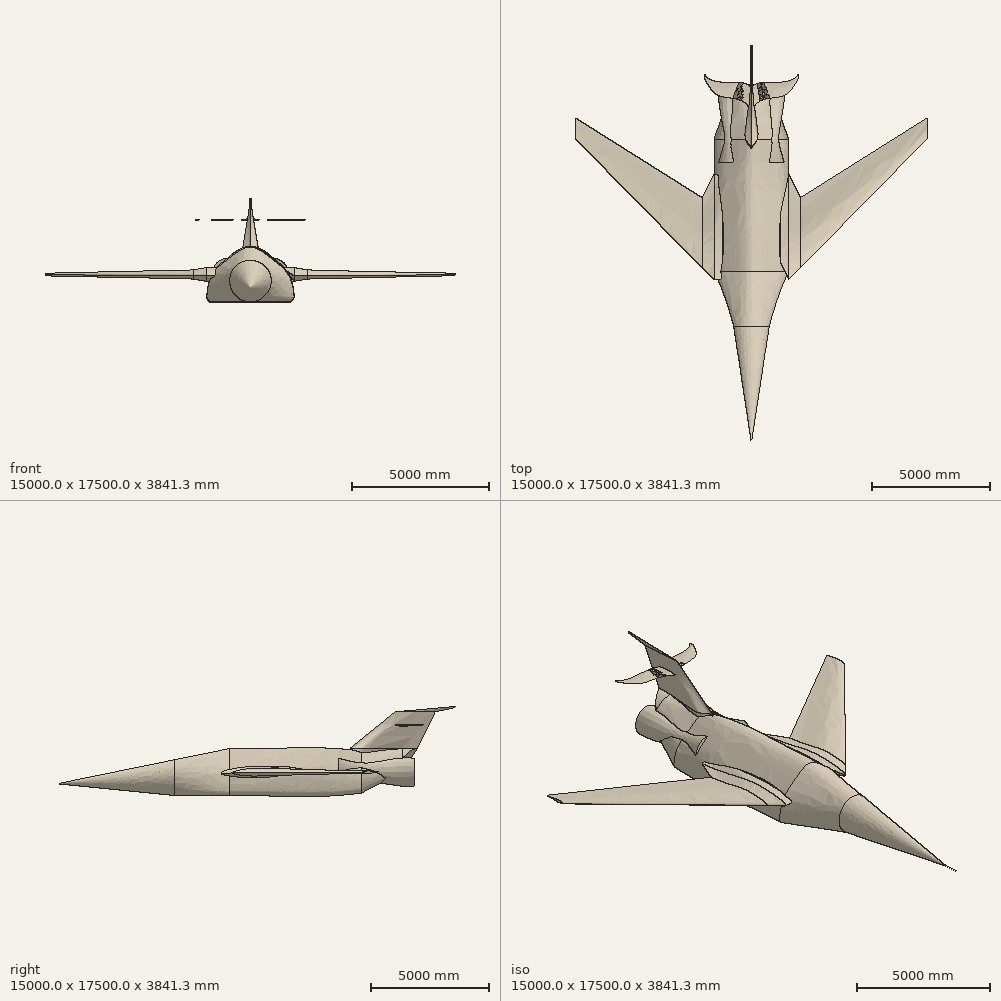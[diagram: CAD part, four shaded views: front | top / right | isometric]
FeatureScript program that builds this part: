
annotation { "Feature Type Name" : "Feature", "Feature Type Description" : "" }
export const myFeature = defineFeature(function(context is Context, id is Id, definition is map)
    precondition{}
    {
        {
            var Q0;
            Q0=qCreatedBy(makeId("Right.planeOp"),FACE);
            var sketch = newSketch(context, id + "F0", { "sketchPlane" : qUnion([Q0])});
            skLineSegment(sketch, "E0", {"start": v(0, 0) * mm, "end": v(-1750, 0) * mm});
            skLineSegment(sketch, "E1", {"start": v(-1750, 0) * mm, "end": v(-3500, 0) * mm});
            skLineSegment(sketch, "E2", {"start": v(-3500, 0) * mm, "end": v(-3500, -1000) * mm});
            skLineSegment(sketch, "E3", {"start": v(-3500, -1000) * mm, "end": v(-8500, -1000) * mm});
            skLineSegment(sketch, "E4", {"start": v(-8500, -1000) * mm, "end": v(-8500, -499.31) * mm});
            skLineSegment(sketch, "E5", {"start": v(-1151.4, 0) * mm, "end": v(-1151.4, 1000) * mm});
            skLineSegment(sketch, "E6", {"start": v(-1151.4, 1000) * mm, "end": v(-8500, -499.31) * mm});
            skLineSegment(sketch, "E7", {"start": v(-8500, -499.31) * mm, "end": v(-3500, -1000) * mm});
            skLineSegment(sketch, "E8", {"start": v(-3500, 0) * mm, "end": v(-3500, 520.82) * mm});
            skLineSegment(sketch, "E9", {"start": v(-8500, -499.31) * mm, "end": v(-8450, -499.31) * mm});
            skLineSegment(sketch, "E10", {"start": v(-8450, -499.31) * mm, "end": v(-8450, -489.1) * mm});
            skLineSegment(sketch, "E11", {"start": v(-8450, -499.31) * mm, "end": v(-8450, -504.32) * mm});
            skSolve(sketch);
        }
        {
            var Q0;
            Q0=sQuery(id+"F0.wireOp",EDGE,"E5");
            cPlane(context, id + "F1", {"entities" : qUnion([Q0]), "cplaneType" : CPlaneType.LINE_ANGLE, "offset" : 25 * mm, "angle" : 90 * degree, "oppositeDirection" : true, "width" : 150 * mm, "height" : 150 * mm});
        }
        {
            var Q0;
            Q0=qCreatedBy(id+"F1.planeOp",FACE);
            var sketch = newSketch(context, id + "F2", { "sketchPlane" : qUnion([Q0])});
            skLineSegment(sketch, "E12.top", {"start": v(-1394.2, -1000) * mm, "end": v(1394.2, -1000) * mm});
            skPoint(sketch, "E12.middle", {"position": v(0, 0) * mm});
            skFitSpline(sketch, "E13", {"points": [v(-1600, -1000) * mm, v(-848, 530) * mm, v(0, 1000) * mm, v(848, 530) * mm, v(1600, -1000) * mm], "startDerivative": vector(0, 10524.75) * mm, "endDerivative": vector(0, -10524.75) * mm});
            skArc(sketch, "E14", {"start": v(-735.27, 618.52) * mm, "mid": v(-1273.27, 435.52) * mm, "end": v(-1440.68, -107.53) * mm});
            skArc(sketch, "E15", {"start": v(1440.68, -107.53) * mm, "mid": v(1273.27, 435.52) * mm, "end": v(735.27, 618.52) * mm});
            skFitSpline(sketch, "E16.trimOffspring", {"points": [v(-1600, -1000) * mm, v(-848, 530) * mm, v(0, 1000) * mm, v(848, 530) * mm, v(1600, -1000) * mm], "startDerivative": vector(0, 10524.75) * mm, "endDerivative": vector(0, -10524.75) * mm});
            skFitSpline(sketch, "E17.trimOffspring", {"points": [v(-1600, -1000) * mm, v(-848, 530) * mm, v(0, 1000) * mm, v(848, 530) * mm, v(1600, -1000) * mm], "startDerivative": vector(0, 10524.75) * mm, "endDerivative": vector(0, -10524.75) * mm});
            skArc(sketch, "E18.filletArc", {"start": v(-1593.82, -787.83) * mm, "mid": v(-1539.85, -937.05) * mm, "end": v(-1394.2, -1000) * mm});
            skArc(sketch, "E19.filletArc", {"start": v(1394.2, -1000) * mm, "mid": v(1539.85, -937.05) * mm, "end": v(1593.82, -787.83) * mm});
            skSolve(sketch);
        }
        {
            var Q0;
            Q0=qCreatedBy(makeId("Front.planeOp"),FACE);
            var sketch = newSketch(context, id + "F3", { "sketchPlane" : qUnion([Q0])});
            skLineSegment(sketch, "E20.top", {"start": v(-1394.2, -1000) * mm, "end": v(1394.2, -1000) * mm});
            skPoint(sketch, "E20.middle", {"position": v(0, 0) * mm});
            skFitSpline(sketch, "E21", {"points": [v(-1600, -1000) * mm, v(-848, 530) * mm, v(0, 1000) * mm, v(848, 530) * mm, v(1600, -1000) * mm], "startDerivative": vector(0, 10524.75) * mm, "endDerivative": vector(0, -10524.75) * mm});
            skArc(sketch, "E22", {"start": v(-735.27, 618.52) * mm, "mid": v(-1273.27, 435.52) * mm, "end": v(-1440.68, -107.53) * mm});
            skArc(sketch, "E23", {"start": v(1440.68, -107.53) * mm, "mid": v(1273.27, 435.52) * mm, "end": v(735.27, 618.52) * mm});
            skFitSpline(sketch, "E24.trimOffspring", {"points": [v(-1600, -1000) * mm, v(-848, 530) * mm, v(0, 1000) * mm, v(848, 530) * mm, v(1600, -1000) * mm], "startDerivative": vector(0, 10524.75) * mm, "endDerivative": vector(0, -10524.75) * mm});
            skFitSpline(sketch, "E25.trimOffspring", {"points": [v(-1600, -1000) * mm, v(-848, 530) * mm, v(0, 1000) * mm, v(848, 530) * mm, v(1600, -1000) * mm], "startDerivative": vector(0, 10524.75) * mm, "endDerivative": vector(0, -10524.75) * mm});
            skArc(sketch, "E26.filletArc", {"start": v(-1593.82, -787.83) * mm, "mid": v(-1539.85, -937.05) * mm, "end": v(-1394.2, -1000) * mm});
            skArc(sketch, "E27.filletArc", {"start": v(1394.2, -1000) * mm, "mid": v(1539.85, -937.05) * mm, "end": v(1593.82, -787.83) * mm});
            skSolve(sketch);
        }
        {
            var Q0;
            Q0=qCreatedBy(makeId("Front.planeOp"),FACE);
            cPlane(context, id + "F4", {"entities" : qUnion([Q0]), "cplaneType" : CPlaneType.OFFSET, "offset" : 3500 * mm, "oppositeDirection" : true, "width" : 150 * mm, "height" : 150 * mm});
        }
        {
            var Q0;
            Q0=qCreatedBy(id+"F4.planeOp",FACE);
            var sketch = newSketch(context, id + "F5", { "sketchPlane" : qUnion([Q0])});
            skLineSegment(sketch, "E28.top", {"start": v(-1394.2, -1000) * mm, "end": v(1394.2, -1000) * mm});
            skPoint(sketch, "E28.middle", {"position": v(0, 0) * mm});
            skFitSpline(sketch, "E29", {"points": [v(-1600, -1000) * mm, v(-848, 530) * mm, v(0, 1000) * mm, v(848, 530) * mm, v(1600, -1000) * mm], "startDerivative": vector(0, 10524.75) * mm, "endDerivative": vector(0, -10524.75) * mm});
            skArc(sketch, "E30", {"start": v(-735.27, 618.52) * mm, "mid": v(-1273.27, 435.52) * mm, "end": v(-1440.68, -107.53) * mm});
            skArc(sketch, "E31", {"start": v(1440.68, -107.53) * mm, "mid": v(1273.27, 435.52) * mm, "end": v(735.27, 618.52) * mm});
            skFitSpline(sketch, "E32.trimOffspring", {"points": [v(-1600, -1000) * mm, v(-848, 530) * mm, v(0, 1000) * mm, v(848, 530) * mm, v(1600, -1000) * mm], "startDerivative": vector(0, 10524.75) * mm, "endDerivative": vector(0, -10524.75) * mm});
            skFitSpline(sketch, "E33.trimOffspring", {"points": [v(-1600, -1000) * mm, v(-848, 530) * mm, v(0, 1000) * mm, v(848, 530) * mm, v(1600, -1000) * mm], "startDerivative": vector(0, 10524.75) * mm, "endDerivative": vector(0, -10524.75) * mm});
            skArc(sketch, "E34.filletArc", {"start": v(-1593.82, -787.83) * mm, "mid": v(-1539.85, -937.05) * mm, "end": v(-1394.2, -1000) * mm});
            skArc(sketch, "E35.filletArc", {"start": v(1394.2, -1000) * mm, "mid": v(1539.85, -937.05) * mm, "end": v(1593.82, -787.83) * mm});
            skSolve(sketch);
        }
        {
            var Q0;
            Q0=qCreatedBy(makeId("Front.planeOp"),FACE);
            cPlane(context, id + "F6", {"entities" : qUnion([Q0]), "cplaneType" : CPlaneType.OFFSET, "offset" : 4500 * mm, "oppositeDirection" : true, "width" : 150 * mm, "height" : 150 * mm});
        }
        {
            var Q0;
            Q0=qCreatedBy(id+"F6.planeOp",FACE);
            var sketch = newSketch(context, id + "F7", { "sketchPlane" : qUnion([Q0])});
            skLineSegment(sketch, "E36.top", {"start": v(-1413.07, -900) * mm, "end": v(1413.07, -900) * mm});
            skPoint(sketch, "E36.middle", {"position": v(0, 0) * mm});
            skFitSpline(sketch, "E37", {"points": [v(-1600, -900) * mm, v(-784.42, 441.24) * mm, v(0, 900) * mm, v(784.42, 441.24) * mm, v(1600, -900) * mm], "startDerivative": vector(0, 9508.62) * mm, "endDerivative": vector(0, -9508.62) * mm});
            skArc(sketch, "E38", {"start": v(-719.25, 488.69) * mm, "mid": v(-1131.76, 394.84) * mm, "end": v(-1324.66, 18.33) * mm});
            skArc(sketch, "E39", {"start": v(1324.66, 18.33) * mm, "mid": v(1131.76, 394.84) * mm, "end": v(719.25, 488.69) * mm});
            skFitSpline(sketch, "E40.trimOffspring", {"points": [v(-1600, -900) * mm, v(-784.42, 441.24) * mm, v(0, 900) * mm, v(784.42, 441.24) * mm, v(1600, -900) * mm], "startDerivative": vector(0, 9508.62) * mm, "endDerivative": vector(0, -9508.62) * mm});
            skFitSpline(sketch, "E41.trimOffspring", {"points": [v(-1600, -900) * mm, v(-784.42, 441.24) * mm, v(0, 900) * mm, v(784.42, 441.24) * mm, v(1600, -900) * mm], "startDerivative": vector(0, 9508.62) * mm, "endDerivative": vector(0, -9508.62) * mm});
            skArc(sketch, "E42.filletArc", {"start": v(-1592.48, -705.43) * mm, "mid": v(-1545.4, -842.02) * mm, "end": v(-1413.07, -900) * mm});
            skArc(sketch, "E43.filletArc", {"start": v(1413.07, -900) * mm, "mid": v(1545.4, -842.02) * mm, "end": v(1592.48, -705.43) * mm});
            skLineSegment(sketch, "E44", {"start": v(-719.25, 488.69) * mm, "end": v(-1324.66, 18.33) * mm, "construction": true});
            skLineSegment(sketch, "E45", {"start": v(719.25, 488.69) * mm, "end": v(1324.66, 18.33) * mm, "construction": true});
            skSolve(sketch);
        }
        {
            var Q0;
            Q0=qCreatedBy(makeId("Front.planeOp"),FACE);
            cPlane(context, id + "F8", {"entities" : qUnion([Q0]), "cplaneType" : CPlaneType.OFFSET, "offset" : 6232.05 * mm, "oppositeDirection" : true, "width" : 150 * mm, "height" : 150 * mm});
        }
        {
            var Q0;
            Q0=qCreatedBy(id+"F8.planeOp",FACE);
            var sketch = newSketch(context, id + "F9", { "sketchPlane" : qUnion([Q0])});
            skArc(sketch, "E46", {"start": v(998.61, 52.63) * mm, "mid": v(0, 1000) * mm, "end": v(-998.61, 52.63) * mm});
            skLineSegment(sketch, "E47", {"start": v(0, 0) * mm, "end": v(-948.68, 0) * mm});
            skLineSegment(sketch, "E48", {"start": v(0, 0) * mm, "end": v(948.68, 0) * mm});
            skLineSegment(sketch, "E49", {"start": v(0, 1000) * mm, "end": v(0, 675) * mm, "construction": true});
            skLineSegment(sketch, "E50", {"start": v(0, 675) * mm, "end": v(-737.82, 675) * mm, "construction": true});
            skLineSegment(sketch, "E51", {"start": v(0, 675) * mm, "end": v(737.82, 675) * mm, "construction": true});
            skPoint(sketch, "E52.visualSharp", {"position": v(-1000, 0) * mm});
            skArc(sketch, "E52.filletArc", {"start": v(-998.61, 52.63) * mm, "mid": v(-984.96, 15.59) * mm, "end": v(-948.68, 0) * mm});
            skPoint(sketch, "E53.visualSharp", {"position": v(1000, 0) * mm});
            skArc(sketch, "E53.filletArc", {"start": v(948.68, 0) * mm, "mid": v(984.96, 15.59) * mm, "end": v(998.61, 52.63) * mm});
            skSolve(sketch);
        }
        {
            var Q0;
            Q0=makeQuery(id+"F2.imprint","IMPRINT",FACE,{"disambiguationData":[TD([[makeQuery(id+"F2.imprint","IMPRINT",EDGE,{"derivedFrom":sQuery(id+"F2.wireOp",EDGE,"E12.top")}),1.0]])]});
            var Q1;
            Q1=makeQuery(id+"F3.imprint","IMPRINT",FACE,{"disambiguationData":[TD([[makeQuery(id+"F3.imprint","IMPRINT",EDGE,{"derivedFrom":sQuery(id+"F3.wireOp",EDGE,"E20.top")}),1.0]])]});
            var Q2;
            Q2=makeQuery(id+"F5.imprint","IMPRINT",FACE,{"disambiguationData":[TD([[makeQuery(id+"F5.imprint","IMPRINT",EDGE,{"derivedFrom":sQuery(id+"F5.wireOp",EDGE,"E28.top")}),1.0]])]});
            var Q3;
            Q3=makeQuery(id+"F7.imprint","IMPRINT",FACE,{"disambiguationData":[TD([[makeQuery(id+"F7.imprint","IMPRINT",EDGE,{"derivedFrom":sQuery(id+"F7.wireOp",EDGE,"E36.top")}),1.0]])]});
            loft(context, id + "F10", {"sheetProfilesArray" : [{ "sheetProfileEntities" : qUnion([Q0]) }, { "sheetProfileEntities" : qUnion([Q1]) }, { "sheetProfileEntities" : qUnion([Q2]) }, { "sheetProfileEntities" : qUnion([Q3]) }]});
        }
        {
            var Q0;
            Q0=sQuery(id+"F7.wireOp",EDGE,"E44");
            var Q1;
            Q1=sQuery(id+"F9.wireOp",VERTEX,"E50.end");
            cPlane(context, id + "F11", {"entities" : qUnion([Q0, Q1]), "cplaneType" : CPlaneType.LINE_ANGLE, "offset" : 25 * mm, "angle" : 180 * degree, "width" : 150 * mm, "height" : 150 * mm});
        }
        {
            var Q0;
            Q0=qCreatedBy(id+"F11.planeOp",FACE);
            var sketch = newSketch(context, id + "F12", { "sketchPlane" : qUnion([Q0])});
            skLineSegment(sketch, "E54", {"start": v(-589.34, 4526.34) * mm, "end": v(-612.8, 6268.32) * mm});
            skLineSegment(sketch, "E55", {"start": v(-1354.08, 4472.19) * mm, "end": v(-612.8, 6268.32) * mm});
            skSolve(sketch);
        }
        {
            var Q0;
            Q0=sQuery(id+"F7.wireOp",EDGE,"E45");
            var Q1;
            Q1=sQuery(id+"F9.wireOp",VERTEX,"E51.end");
            cPlane(context, id + "F13", {"entities" : qUnion([Q0, Q1]), "cplaneType" : CPlaneType.LINE_ANGLE, "offset" : 25 * mm, "angle" : 0 * degree, "width" : 150 * mm, "height" : 150 * mm});
        }
        {
            var Q0;
            Q0=qCreatedBy(id+"F13.planeOp",FACE);
            var sketch = newSketch(context, id + "F14", { "sketchPlane" : qUnion([Q0])});
            skLineSegment(sketch, "E56", {"start": v(589.34, 4526.34) * mm, "end": v(612.8, 6268.32) * mm});
            skLineSegment(sketch, "E57", {"start": v(1354.08, 4472.19) * mm, "end": v(612.8, 6268.32) * mm});
            skSolve(sketch);
        }
        {
            var Q1;
            Q1=makeQuery(id+"F10.opLoft","CAP_FACE",FACE,{"disambiguationData":[OSD([makeQuery(id+"F7.imprint","IMPRINT",FACE,{"disambiguationData":[TD([[makeQuery(id+"F7.imprint","IMPRINT",EDGE,{"derivedFrom":sQuery(id+"F7.wireOp",EDGE,"E36.top")}),1.0]])]})])],"isStart":true});
            var Q2;
            Q2=makeQuery(id+"F9.imprint","IMPRINT",FACE,{"disambiguationData":[TD([[makeQuery(id+"F9.imprint","IMPRINT",EDGE,{"derivedFrom":sQuery(id+"F9.wireOp",EDGE,"E46")}),1.0]])]});
            var Q3;
            Q3=sQuery(id+"F12.wireOp",EDGE,"E54");
            var Q4;
            Q4=sQuery(id+"F14.wireOp",EDGE,"E56");
            loft(context, id + "F15", {"operationType" : NewBodyOperationType.ADD, "addGuides" : true, "sheetProfilesArray" : [{ "sheetProfileEntities" : qUnion([Q1]) }, { "sheetProfileEntities" : qUnion([Q2]) }], "guidesArray" : [{ "guideEntities" : qUnion([Q3]), "guideDerivativeType" : LoftGuideDerivativeType.DEFAULT, "guideDerivativeMagnitude" : 1 }, { "guideEntities" : qUnion([Q4]), "guideDerivativeType" : LoftGuideDerivativeType.DEFAULT, "guideDerivativeMagnitude" : 1 }]});
        }
        {
            var Q0;
            Q0=makeQuery(id+"F15.opLoft","CAP_FACE",FACE,{"disambiguationData":[OSD([makeQuery(id+"F9.imprint","IMPRINT",FACE,{"disambiguationData":[TD([[makeQuery(id+"F9.imprint","IMPRINT",EDGE,{"derivedFrom":sQuery(id+"F9.wireOp",EDGE,"E46")}),1.0]])]})])],"isStart":true});
            extrude(context, id + "F16", {"entities" : qUnion([Q0]), "operationType" : NewBodyOperationType.ADD, "depth" : 649.4 * mm, "offsetDistance" : 25 * mm});
        }
        {
            var Q0;
            Q0=qCreatedBy(makeId("Right.planeOp"),FACE);
            var sketch = newSketch(context, id + "F17", { "sketchPlane" : qUnion([Q0])});
            skLineSegment(sketch, "E58", {"start": v(0, 0) * mm, "end": v(4500, 0) * mm});
            skLineSegment(sketch, "E59", {"start": v(4500, 0) * mm, "end": v(6232.05, 0) * mm});
            skLineSegment(sketch, "E60", {"start": v(4500, 0) * mm, "end": v(4500, 1000) * mm});
            skLineSegment(sketch, "E61", {"start": v(4500, 1000) * mm, "end": v(6881.46, 1000) * mm});
            skLineSegment(sketch, "E62", {"start": v(6881.46, 1000) * mm, "end": v(6881.46, -1000) * mm});
            skLineSegment(sketch, "E63", {"start": v(6881.46, 1000) * mm, "end": v(6232.05, 0) * mm});
            skLineSegment(sketch, "E64", {"start": v(6232.05, 0) * mm, "end": v(5582.64, -1000) * mm});
            skLineSegment(sketch, "E65", {"start": v(5582.64, -1000) * mm, "end": v(6881.46, -1000) * mm});
            skSolve(sketch);
        }
        {
            var Q0;
            Q0=makeQuery(id+"F17.imprint","IMPRINT",FACE,{"disambiguationData":[TD([[makeQuery(id+"F17.imprint","IMPRINT",EDGE,{"derivedFrom":sQuery(id+"F17.wireOp",EDGE,"E62")}),-1.0]])]});
            var Q1;
            Q1=sQuery(id+"F17.wireOp",EDGE,"E61");
            revolve(context, id + "F18", {"operationType" : NewBodyOperationType.REMOVE, "entities" : qUnion([Q0]), "axis" : qUnion([Q1]), "revolveType" : RevolveType.SYMMETRIC, "oppositeDirection" : true, "angle" : 182 * degree});
        }
        {
            var Q0;
            Q0=qCreatedBy(id+"F1.planeOp",FACE);
            var sketch = newSketch(context, id + "F19", { "sketchPlane" : qUnion([Q0])});
            skLineSegment(sketch, "E66.top", {"start": v(-1394.2, -1000) * mm, "end": v(1394.2, -1000) * mm});
            skPoint(sketch, "E66.middle", {"position": v(0, 0) * mm});
            skFitSpline(sketch, "E67", {"points": [v(-1600, -1000) * mm, v(-848, 530) * mm, v(0, 1000) * mm, v(848, 530) * mm, v(1600, -1000) * mm], "startDerivative": vector(0, 10524.75) * mm, "endDerivative": vector(0, -10524.75) * mm});
            skArc(sketch, "E68.filletArc", {"start": v(-1593.82, -787.83) * mm, "mid": v(-1539.85, -937.05) * mm, "end": v(-1394.2, -1000) * mm});
            skArc(sketch, "E69.filletArc", {"start": v(1394.2, -1000) * mm, "mid": v(1539.85, -937.05) * mm, "end": v(1593.82, -787.83) * mm});
            skLineSegment(sketch, "E70", {"start": v(-1593.82, -787.83) * mm, "end": v(-1394.2, -1000) * mm, "construction": true});
            skLineSegment(sketch, "E71", {"start": v(1593.82, -787.83) * mm, "end": v(1394.2, -1000) * mm, "construction": true});
            skSolve(sketch);
        }
        {
            var Q0;
            Q0=qCreatedBy(makeId("Front.planeOp"),FACE);
            cPlane(context, id + "F20", {"entities" : qUnion([Q0]), "cplaneType" : CPlaneType.OFFSET, "offset" : 3500 * mm, "width" : 150 * mm, "height" : 150 * mm});
        }
        {
            var Q0;
            Q0=qCreatedBy(id+"F20.planeOp",FACE);
            var sketch = newSketch(context, id + "F21", { "sketchPlane" : qUnion([Q0])});
            skCircle(sketch, "E72", {"center": v(0, -239.59) * mm, "radius": 760.41 * mm});
            skLineSegment(sketch, "E73", {"start": v(0, -1000) * mm, "end": v(0, -800) * mm, "construction": true});
            skLineSegment(sketch, "E74", {"start": v(0, -800) * mm, "end": v(-513.97, -800) * mm, "construction": true});
            skLineSegment(sketch, "E75", {"start": v(0, -800) * mm, "end": v(513.97, -800) * mm, "construction": true});
            skSolve(sketch);
        }
        {
            var Q0;
            Q0=qCreatedBy(makeId("Front.planeOp"),FACE);
            cPlane(context, id + "F22", {"entities" : qUnion([Q0]), "cplaneType" : CPlaneType.OFFSET, "offset" : 8450 * mm, "width" : 150 * mm, "height" : 150 * mm});
        }
        {
            var Q0;
            Q0=qCreatedBy(id+"F22.planeOp",FACE);
            var sketch = newSketch(context, id + "F23", { "sketchPlane" : qUnion([Q0])});
            skCircle(sketch, "E76", {"center": v(0, -496.71) * mm, "radius": 7.6 * mm});
            skSolve(sketch);
        }
        {
            var Q0;
            Q0=sQuery(id+"F19.wireOp",EDGE,"E70");
            var Q1;
            Q1=sQuery(id+"F21.wireOp",VERTEX,"E74.end");
            cPlane(context, id + "F24", {"entities" : qUnion([Q0, Q1]), "cplaneType" : CPlaneType.LINE_ANGLE, "offset" : 25 * mm, "angle" : 0 * degree, "width" : 150 * mm, "height" : 150 * mm});
        }
        {
            var Q0;
            Q0=qCreatedBy(id+"F24.planeOp",FACE);
            var sketch = newSketch(context, id + "F25", { "sketchPlane" : qUnion([Q0])});
            skLineSegment(sketch, "E77", {"start": v(3032.27, -230.44) * mm, "end": v(558.11, 518.4) * mm});
            skLineSegment(sketch, "E78", {"start": v(3032.27, -230.44) * mm, "end": v(558.11, 227.09) * mm});
            skSolve(sketch);
        }
        {
            var Q0;
            Q0=sQuery(id+"F19.wireOp",EDGE,"E71");
            var Q1;
            Q1=sQuery(id+"F21.wireOp",VERTEX,"E75.end");
            cPlane(context, id + "F26", {"entities" : qUnion([Q0, Q1]), "cplaneType" : CPlaneType.LINE_ANGLE, "offset" : 25 * mm, "angle" : 180 * degree, "width" : 150 * mm, "height" : 150 * mm});
        }
        {
            var Q0;
            Q0=qCreatedBy(id+"F26.planeOp",FACE);
            var sketch = newSketch(context, id + "F27", { "sketchPlane" : qUnion([Q0])});
            skLineSegment(sketch, "E79", {"start": v(-3032.27, -230.44) * mm, "end": v(-558.11, 518.4) * mm});
            skLineSegment(sketch, "E80", {"start": v(-3032.27, -230.44) * mm, "end": v(-558.11, 227.09) * mm});
            skSolve(sketch);
        }
        {
            var Q1;
            Q1=makeQuery(id+"F19.imprint","IMPRINT",FACE,{"disambiguationData":[TD([[makeQuery(id+"F19.imprint","IMPRINT",EDGE,{"derivedFrom":sQuery(id+"F19.wireOp",EDGE,"E66.top")}),1.0]])]});
            var Q2;
            Q2=makeQuery(id+"F21.imprint","IMPRINT",FACE,{"disambiguationData":[TD([[makeQuery(id+"F21.imprint","IMPRINT",EDGE,{"derivedFrom":sQuery(id+"F21.wireOp",EDGE,"E72")}),1.0]])]});
            var Q3;
            Q3=sQuery(id+"F25.wireOp",EDGE,"E77");
            var Q4;
            Q4=sQuery(id+"F27.wireOp",EDGE,"E79");
            loft(context, id + "F28", {"operationType" : NewBodyOperationType.ADD, "addGuides" : true, "sheetProfilesArray" : [{ "sheetProfileEntities" : qUnion([Q1]) }, { "sheetProfileEntities" : qUnion([Q2]) }], "guidesArray" : [{ "guideEntities" : qUnion([Q3]), "guideDerivativeType" : LoftGuideDerivativeType.DEFAULT, "guideDerivativeMagnitude" : 1 }, { "guideEntities" : qUnion([Q4]), "guideDerivativeType" : LoftGuideDerivativeType.DEFAULT, "guideDerivativeMagnitude" : 1 }]});
        }
        {
            var Q1;
            Q1=makeQuery(id+"F28.opLoft","CAP_FACE",FACE,{"disambiguationData":[OSD([makeQuery(id+"F21.imprint","IMPRINT",FACE,{"disambiguationData":[TD([[makeQuery(id+"F21.imprint","IMPRINT",EDGE,{"derivedFrom":sQuery(id+"F21.wireOp",EDGE,"E72")}),1.0]])]})])],"isStart":true});
            var Q2;
            Q2=makeQuery(id+"F23.imprint","IMPRINT",FACE,{"disambiguationData":[TD([[makeQuery(id+"F23.imprint","IMPRINT",EDGE,{"derivedFrom":sQuery(id+"F23.wireOp",EDGE,"E76")}),1.0]])]});
            loft(context, id + "F29", {"operationType" : NewBodyOperationType.ADD, "sheetProfilesArray" : [{ "sheetProfileEntities" : qUnion([Q1]) }, { "sheetProfileEntities" : qUnion([Q2]) }]});
        }
        {
            var Q0;
            Q0=makeQuery(id+"F29.opLoft","CAP_FACE",FACE,{"disambiguationData":[OSD([makeQuery(id+"F23.imprint","IMPRINT",FACE,{"disambiguationData":[TD([[makeQuery(id+"F23.imprint","IMPRINT",EDGE,{"derivedFrom":sQuery(id+"F23.wireOp",EDGE,"E76")}),1.0]])]})])],"isStart":true});
            extrude(context, id + "F30", {"entities" : qUnion([Q0]), "operationType" : NewBodyOperationType.ADD, "depth" : 550 * mm, "offsetDistance" : 25 * mm});
        }
        {
            var Q0;
            Q0=qCreatedBy(makeId("Front.planeOp"),FACE);
            cPlane(context, id + "F31", {"entities" : qUnion([Q0]), "cplaneType" : CPlaneType.OFFSET, "offset" : 3500 * mm, "oppositeDirection" : true, "width" : 150 * mm, "height" : 150 * mm});
        }
        {
            var Q0;
            Q0=qCreatedBy(id+"F31.planeOp",FACE);
            var sketch = newSketch(context, id + "F32", { "sketchPlane" : qUnion([Q0])});
            skCircle(sketch, "E81", {"center": v(-800, 0) * mm, "radius": 600 * mm});
            skCircle(sketch, "E82", {"center": v(800, 0) * mm, "radius": 600 * mm});
            skSolve(sketch);
        }
        {
            var Q0;
            Q0=qCreatedBy(makeId("Front.planeOp"),FACE);
            cPlane(context, id + "F33", {"entities" : qUnion([Q0]), "cplaneType" : CPlaneType.OFFSET, "offset" : 4500 * mm, "oppositeDirection" : true, "width" : 150 * mm, "height" : 150 * mm});
        }
        {
            var Q0;
            Q0=qCreatedBy(id+"F33.planeOp",FACE);
            var sketch = newSketch(context, id + "F34", { "sketchPlane" : qUnion([Q0])});
            skCircle(sketch, "E83", {"center": v(-800, 0) * mm, "radius": 400 * mm});
            skCircle(sketch, "E84", {"center": v(800, 0) * mm, "radius": 400 * mm});
            skSolve(sketch);
        }
        {
            var Q0;
            Q0=qCreatedBy(makeId("Front.planeOp"),FACE);
            cPlane(context, id + "F35", {"entities" : qUnion([Q0]), "cplaneType" : CPlaneType.OFFSET, "offset" : 6232.05 * mm, "oppositeDirection" : true, "width" : 150 * mm, "height" : 150 * mm});
        }
        {
            var Q0;
            Q0=qCreatedBy(id+"F35.planeOp",FACE);
            var sketch = newSketch(context, id + "F36", { "sketchPlane" : qUnion([Q0])});
            skCircle(sketch, "E85", {"center": v(-800, 0) * mm, "radius": 600 * mm});
            skCircle(sketch, "E86", {"center": v(800, 0) * mm, "radius": 600 * mm});
            skSolve(sketch);
        }
        {
            var Q0;
            Q0=qCreatedBy(makeId("Front.planeOp"),FACE);
            cPlane(context, id + "F37", {"entities" : qUnion([Q0]), "cplaneType" : CPlaneType.OFFSET, "offset" : 6732.05 * mm, "oppositeDirection" : true, "width" : 150 * mm, "height" : 150 * mm});
        }
        {
            var Q0;
            Q0=qCreatedBy(id+"F37.planeOp",FACE);
            var sketch = newSketch(context, id + "F38", { "sketchPlane" : qUnion([Q0])});
            skCircle(sketch, "E87", {"center": v(-800, 0) * mm, "radius": 600 * mm});
            skCircle(sketch, "E88", {"center": v(800, 0) * mm, "radius": 600 * mm});
            skSolve(sketch);
        }
        {
            var Q0;
            Q0=makeQuery(id+"F32.imprint","IMPRINT",FACE,{"disambiguationData":[TD([[makeQuery(id+"F32.imprint","IMPRINT",EDGE,{"derivedFrom":sQuery(id+"F32.wireOp",EDGE,"E81")}),1.0]])]});
            var Q1;
            Q1=makeQuery(id+"F34.imprint","IMPRINT",FACE,{"disambiguationData":[TD([[makeQuery(id+"F34.imprint","IMPRINT",EDGE,{"derivedFrom":sQuery(id+"F34.wireOp",EDGE,"E83")}),1.0]])]});
            var Q2;
            Q2=makeQuery(id+"F36.imprint","IMPRINT",FACE,{"disambiguationData":[TD([[makeQuery(id+"F36.imprint","IMPRINT",EDGE,{"derivedFrom":sQuery(id+"F36.wireOp",EDGE,"E85")}),1.0]])]});
            var Q3;
            Q3=makeQuery(id+"F38.imprint","IMPRINT",FACE,{"disambiguationData":[TD([[makeQuery(id+"F38.imprint","IMPRINT",EDGE,{"derivedFrom":sQuery(id+"F38.wireOp",EDGE,"E87")}),1.0]])]});
            loft(context, id + "F39", {"sheetProfilesArray" : [{ "sheetProfileEntities" : qUnion([Q0]) }, { "sheetProfileEntities" : qUnion([Q1]) }, { "sheetProfileEntities" : qUnion([Q2]) }, { "sheetProfileEntities" : qUnion([Q3]) }]});
        }
        {
            var Q0;
            Q0=makeQuery(id+"F32.imprint","IMPRINT",FACE,{"disambiguationData":[TD([[makeQuery(id+"F32.imprint","IMPRINT",EDGE,{"derivedFrom":sQuery(id+"F32.wireOp",EDGE,"E82")}),1.0]])]});
            var Q1;
            Q1=makeQuery(id+"F34.imprint","IMPRINT",FACE,{"disambiguationData":[TD([[makeQuery(id+"F34.imprint","IMPRINT",EDGE,{"derivedFrom":sQuery(id+"F34.wireOp",EDGE,"E84")}),1.0]])]});
            var Q2;
            Q2=makeQuery(id+"F36.imprint","IMPRINT",FACE,{"disambiguationData":[TD([[makeQuery(id+"F36.imprint","IMPRINT",EDGE,{"derivedFrom":sQuery(id+"F36.wireOp",EDGE,"E86")}),1.0]])]});
            var Q3;
            Q3=makeQuery(id+"F38.imprint","IMPRINT",FACE,{"disambiguationData":[TD([[makeQuery(id+"F38.imprint","IMPRINT",EDGE,{"derivedFrom":sQuery(id+"F38.wireOp",EDGE,"E88")}),1.0]])]});
            loft(context, id + "F40", {"sheetProfilesArray" : [{ "sheetProfileEntities" : qUnion([Q0]) }, { "sheetProfileEntities" : qUnion([Q1]) }, { "sheetProfileEntities" : qUnion([Q2]) }, { "sheetProfileEntities" : qUnion([Q3]) }]});
        }
        {
            var Q0;
            Q0=qCreatedBy(makeId("Right.planeOp"),FACE);
            var sketch = newSketch(context, id + "F41", { "sketchPlane" : qUnion([Q0])});
            skFitSpline(sketch, "E89", {"points": [v(-1500, -50) * mm, v(0, 250) * mm, v(3000, -50) * mm, v(0, -250) * mm, v(-1500, -50) * mm]});
            skSolve(sketch);
        }
        {
            var Q0;
            Q0=qCreatedBy(makeId("Right.planeOp"),FACE);
            cPlane(context, id + "F42", {"entities" : qUnion([Q0]), "cplaneType" : CPlaneType.OFFSET, "offset" : 1600 * mm, "oppositeDirection" : true, "width" : 150 * mm, "height" : 150 * mm});
        }
        {
            var Q0;
            Q0=qCreatedBy(id+"F42.planeOp",FACE);
            var sketch = newSketch(context, id + "F43", { "sketchPlane" : qUnion([Q0])});
            skFitSpline(sketch, "E90", {"points": [v(-1500, -50) * mm, v(0, 250) * mm, v(3000, -50) * mm], "startDerivative": vector(0, 887.04) * mm, "endDerivative": vector(7705.35, -256.85) * mm});
            skFitSpline(sketch, "E91", {"points": [v(-1500, -50) * mm, v(0, -250) * mm, v(3000, -50) * mm], "startDerivative": vector(0, -722.87) * mm, "endDerivative": vector(7692.49, -256.42) * mm});
            skSolve(sketch);
        }
        {
            var Q0;
            Q0=qCreatedBy(makeId("Right.planeOp"),FACE);
            cPlane(context, id + "F44", {"entities" : qUnion([Q0]), "cplaneType" : CPlaneType.OFFSET, "offset" : 1600 * mm, "width" : 150 * mm, "height" : 150 * mm});
        }
        {
            var Q0;
            Q0=qCreatedBy(id+"F44.planeOp",FACE);
            var sketch = newSketch(context, id + "F45", { "sketchPlane" : qUnion([Q0])});
            skFitSpline(sketch, "E92", {"points": [v(-1500, -50) * mm, v(0, 250) * mm, v(3000, -50) * mm], "startDerivative": vector(0, 887.04) * mm, "endDerivative": vector(7705.35, -256.85) * mm});
            skFitSpline(sketch, "E93", {"points": [v(-1500, -50) * mm, v(0, -250) * mm, v(3000, -50) * mm], "startDerivative": vector(0, -722.87) * mm, "endDerivative": vector(7692.49, -256.42) * mm});
            skSolve(sketch);
        }
        {
            var Q0;
            Q0=qCreatedBy(makeId("Right.planeOp"),FACE);
            cPlane(context, id + "F46", {"entities" : qUnion([Q0]), "cplaneType" : CPlaneType.OFFSET, "offset" : 2100 * mm, "oppositeDirection" : true, "width" : 150 * mm, "height" : 150 * mm});
        }
        {
            var Q0;
            Q0=qCreatedBy(id+"F46.planeOp",FACE);
            var sketch = newSketch(context, id + "F47", { "sketchPlane" : qUnion([Q0])});
            skFitSpline(sketch, "E94", {"points": [v(-1000, -36) * mm, v(0, 170) * mm, v(2000, -36) * mm], "startDerivative": vector(0, 576.8) * mm, "endDerivative": vector(5137.83, -184.96) * mm});
            skFitSpline(sketch, "E95", {"points": [v(-1000, -36) * mm, v(0, -170) * mm, v(2000, -36) * mm], "startDerivative": vector(0, -484.31) * mm, "endDerivative": vector(5128.4, -184.62) * mm});
            skSolve(sketch);
        }
        {
            var Q0;
            Q0=qCreatedBy(makeId("Right.planeOp"),FACE);
            cPlane(context, id + "F48", {"entities" : qUnion([Q0]), "cplaneType" : CPlaneType.OFFSET, "offset" : 2100 * mm, "width" : 150 * mm, "height" : 150 * mm});
        }
        {
            var Q0;
            Q0=qCreatedBy(id+"F48.planeOp",FACE);
            var sketch = newSketch(context, id + "F49", { "sketchPlane" : qUnion([Q0])});
            skFitSpline(sketch, "E96", {"points": [v(-1000, -36) * mm, v(0, 170) * mm, v(2000, -36) * mm], "startDerivative": vector(0, 576.8) * mm, "endDerivative": vector(5137.83, -184.96) * mm});
            skFitSpline(sketch, "E97", {"points": [v(-1000, -36) * mm, v(0, -170) * mm, v(2000, -36) * mm], "startDerivative": vector(0, -484.31) * mm, "endDerivative": vector(5128.4, -184.62) * mm});
            skSolve(sketch);
        }
        {
            var Q0;
            Q0=qCreatedBy(makeId("Right.planeOp"),FACE);
            cPlane(context, id + "F50", {"entities" : qUnion([Q0]), "cplaneType" : CPlaneType.OFFSET, "offset" : 7500 * mm, "oppositeDirection" : true, "width" : 150 * mm, "height" : 150 * mm});
        }
        {
            var Q0;
            Q0=qCreatedBy(id+"F50.planeOp",FACE);
            var sketch = newSketch(context, id + "F51", { "sketchPlane" : qUnion([Q0])});
            skFitSpline(sketch, "E98", {"points": [v(4500, -10) * mm, v(4800, 50) * mm, v(5400, -10) * mm], "startDerivative": vector(0, 177.4) * mm, "endDerivative": vector(1541.07, -51.37) * mm});
            skFitSpline(sketch, "E99", {"points": [v(4500, -10) * mm, v(4800, -50) * mm, v(5400, -10) * mm], "startDerivative": vector(0, -144.57) * mm, "endDerivative": vector(1538.5, -51.28) * mm});
            skSolve(sketch);
        }
        {
            var Q0;
            Q0=qCreatedBy(makeId("Right.planeOp"),FACE);
            cPlane(context, id + "F52", {"entities" : qUnion([Q0]), "cplaneType" : CPlaneType.OFFSET, "offset" : 7500 * mm, "width" : 150 * mm, "height" : 150 * mm});
        }
        {
            var Q0;
            Q0=qCreatedBy(id+"F52.planeOp",FACE);
            var sketch = newSketch(context, id + "F53", { "sketchPlane" : qUnion([Q0])});
            skFitSpline(sketch, "E100", {"points": [v(4500, -10) * mm, v(4800, 50) * mm, v(5400, -10) * mm], "startDerivative": vector(0, 177.4) * mm, "endDerivative": vector(1541.07, -51.37) * mm});
            skFitSpline(sketch, "E101", {"points": [v(4500, -10) * mm, v(4800, -50) * mm, v(5400, -10) * mm], "startDerivative": vector(0, -144.57) * mm, "endDerivative": vector(1538.5, -51.28) * mm});
            skSolve(sketch);
        }
        {
            var Q0;
            Q0=qSketchRegion(id+"F41",true);
            extrude(context, id + "F54", {"entities" : qUnion([Q0]), "endBound" : BoundingType.SYMMETRIC, "depth" : 2500 * mm, "offsetDistance" : 25 * mm});
        }
        {
            var Q1;
            Q1=makeQuery(id+"F54.opExtrude","CAP_FACE",FACE,{"disambiguationData":[OSD([sQuery(id+"F41.wireOp",EDGE,"E89")])],"isStart":true});
            var Q2;
            {var subQ0=sQuery(id+"F43.wireOp",EDGE,"E90");Q2=makeQuery(id+"F43.imprint","IMPRINT",FACE,{"disambiguationData":[TD([[makeQuery(id+"F43.imprint","IMPRINT",EDGE,{"derivedFrom":subQ0}),-1.0]])]});}
            loft(context, id + "F55", {"operationType" : NewBodyOperationType.ADD, "sheetProfilesArray" : [{ "sheetProfileEntities" : qUnion([Q1]) }, { "sheetProfileEntities" : qUnion([Q2]) }]});
        }
        {
            var Q1;
            Q1=makeQuery(id+"F54.opExtrude","CAP_FACE",FACE,{"disambiguationData":[OSD([sQuery(id+"F41.wireOp",EDGE,"E89")])],"isStart":false});
            var Q2;
            {var subQ0=sQuery(id+"F45.wireOp",EDGE,"E92");Q2=makeQuery(id+"F45.imprint","IMPRINT",FACE,{"disambiguationData":[TD([[makeQuery(id+"F45.imprint","IMPRINT",EDGE,{"derivedFrom":subQ0}),-1.0]])]});}
            loft(context, id + "F56", {"operationType" : NewBodyOperationType.ADD, "sheetProfilesArray" : [{ "sheetProfileEntities" : qUnion([Q1]) }, { "sheetProfileEntities" : qUnion([Q2]) }]});
        }
        {
            var Q1;
            {var subQ0=sQuery(id+"F43.wireOp",EDGE,"E90");Q1=makeQuery(id+"F55.opLoft","CAP_FACE",FACE,{"disambiguationData":[OSD([makeQuery(id+"F43.imprint","IMPRINT",FACE,{"disambiguationData":[TD([[makeQuery(id+"F43.imprint","IMPRINT",EDGE,{"derivedFrom":subQ0}),-1.0]])]})])],"isStart":true});}
            var Q2;
            {var subQ0=sQuery(id+"F47.wireOp",EDGE,"E94");Q2=makeQuery(id+"F47.imprint","IMPRINT",FACE,{"disambiguationData":[TD([[makeQuery(id+"F47.imprint","IMPRINT",EDGE,{"derivedFrom":subQ0}),-1.0]])]});}
            loft(context, id + "F57", {"operationType" : NewBodyOperationType.ADD, "sheetProfilesArray" : [{ "sheetProfileEntities" : qUnion([Q1]) }, { "sheetProfileEntities" : qUnion([Q2]) }]});
        }
        {
            var Q1;
            {var subQ0=sQuery(id+"F45.wireOp",EDGE,"E92");Q1=makeQuery(id+"F56.opLoft","CAP_FACE",FACE,{"disambiguationData":[OSD([makeQuery(id+"F45.imprint","IMPRINT",FACE,{"disambiguationData":[TD([[makeQuery(id+"F45.imprint","IMPRINT",EDGE,{"derivedFrom":subQ0}),-1.0]])]})])],"isStart":true});}
            var Q2;
            {var subQ0=sQuery(id+"F49.wireOp",EDGE,"E96");Q2=makeQuery(id+"F49.imprint","IMPRINT",FACE,{"disambiguationData":[TD([[makeQuery(id+"F49.imprint","IMPRINT",EDGE,{"derivedFrom":subQ0}),-1.0]])]});}
            loft(context, id + "F58", {"operationType" : NewBodyOperationType.ADD, "sheetProfilesArray" : [{ "sheetProfileEntities" : qUnion([Q1]) }, { "sheetProfileEntities" : qUnion([Q2]) }]});
        }
        {
            var Q1;
            {var subQ0=sQuery(id+"F47.wireOp",EDGE,"E94");Q1=makeQuery(id+"F57.opLoft","CAP_FACE",FACE,{"disambiguationData":[OSD([makeQuery(id+"F47.imprint","IMPRINT",FACE,{"disambiguationData":[TD([[makeQuery(id+"F47.imprint","IMPRINT",EDGE,{"derivedFrom":subQ0}),-1.0]])]})])],"isStart":true});}
            var Q2;
            {var subQ0=sQuery(id+"F51.wireOp",EDGE,"E98");Q2=makeQuery(id+"F51.imprint","IMPRINT",FACE,{"disambiguationData":[TD([[makeQuery(id+"F51.imprint","IMPRINT",EDGE,{"derivedFrom":subQ0}),-1.0]])]});}
            loft(context, id + "F59", {"operationType" : NewBodyOperationType.ADD, "sheetProfilesArray" : [{ "sheetProfileEntities" : qUnion([Q1]) }, { "sheetProfileEntities" : qUnion([Q2]) }]});
        }
        {
            var Q1;
            {var subQ0=sQuery(id+"F49.wireOp",EDGE,"E96");Q1=makeQuery(id+"F58.opLoft","CAP_FACE",FACE,{"disambiguationData":[OSD([makeQuery(id+"F49.imprint","IMPRINT",FACE,{"disambiguationData":[TD([[makeQuery(id+"F49.imprint","IMPRINT",EDGE,{"derivedFrom":subQ0}),-1.0]])]})])],"isStart":true});}
            var Q2;
            {var subQ0=sQuery(id+"F53.wireOp",EDGE,"E100");Q2=makeQuery(id+"F53.imprint","IMPRINT",FACE,{"disambiguationData":[TD([[makeQuery(id+"F53.imprint","IMPRINT",EDGE,{"derivedFrom":subQ0}),-1.0]])]});}
            loft(context, id + "F60", {"operationType" : NewBodyOperationType.ADD, "sheetProfilesArray" : [{ "sheetProfileEntities" : qUnion([Q1]) }, { "sheetProfileEntities" : qUnion([Q2]) }]});
        }
        {
            var Q0;
            Q0=qCreatedBy(makeId("Right.planeOp"),FACE);
            var sketch = newSketch(context, id + "F61", { "sketchPlane" : qUnion([Q0])});
            skLineSegment(sketch, "E102", {"start": v(0, 0) * mm, "end": v(4500, 0) * mm});
            skLineSegment(sketch, "E103", {"start": v(4500, 0) * mm, "end": v(4500, 1000) * mm});
            skLineSegment(sketch, "E104", {"start": v(4500, 1000) * mm, "end": v(4500, 750) * mm});
            skLineSegment(sketch, "E105", {"start": v(4500, 750) * mm, "end": v(4000, 750) * mm});
            skLineSegment(sketch, "E106", {"start": v(4500, 750) * mm, "end": v(6250, 750) * mm});
            skLineSegment(sketch, "E107", {"start": v(4500, 1000) * mm, "end": v(4000, 1000) * mm});
            skLineSegment(sketch, "E108", {"start": v(4500, 1000) * mm, "end": v(6881.46, 1000) * mm});
            skLineSegment(sketch, "E109", {"start": v(6881.46, 1000) * mm, "end": v(8500, 1000) * mm});
            skLineSegment(sketch, "E110", {"start": v(8500, 1000) * mm, "end": v(8500, 2800) * mm});
            skLineSegment(sketch, "E111", {"start": v(6881.46, 1000) * mm, "end": v(7648.6, 2572.89) * mm});
            skLineSegment(sketch, "E112", {"start": v(7648.6, 2572.89) * mm, "end": v(5943.2, 2572.89) * mm});
            skLineSegment(sketch, "E113", {"start": v(5943.2, 2572.89) * mm, "end": v(4000, 1000) * mm});
            skSolve(sketch);
        }
        {
            var Q0;
            Q0=qCreatedBy(makeId("Top.planeOp"),FACE);
            cPlane(context, id + "F62", {"entities" : qUnion([Q0]), "cplaneType" : CPlaneType.OFFSET, "offset" : 750 * mm, "width" : 150 * mm, "height" : 150 * mm});
        }
        {
            var Q0;
            Q0=qCreatedBy(id+"F62.planeOp",FACE);
            var sketch = newSketch(context, id + "F63", { "sketchPlane" : qUnion([Q0])});
            skFitSpline(sketch, "E114", {"points": [v(0, 4000) * mm, v(-250, 4500) * mm, v(0, 6250) * mm], "startDerivative": vector(-889.86, 1147.1) * mm, "endDerivative": vector(737.87, 3164.53) * mm});
            skFitSpline(sketch, "E115", {"points": [v(0, 4000) * mm, v(250, 4500) * mm, v(0, 6250) * mm], "startDerivative": vector(889.86, 1147.1) * mm, "endDerivative": vector(-737.87, 3164.53) * mm});
            skSolve(sketch);
        }
        {
            var Q0;
            Q0=qCreatedBy(makeId("Top.planeOp"),FACE);
            cPlane(context, id + "F64", {"entities" : qUnion([Q0]), "cplaneType" : CPlaneType.OFFSET, "offset" : 1000 * mm, "width" : 150 * mm, "height" : 150 * mm});
        }
        {
            var Q0;
            Q0=qCreatedBy(id+"F64.planeOp",FACE);
            var sketch = newSketch(context, id + "F65", { "sketchPlane" : qUnion([Q0])});
            skFitSpline(sketch, "E116", {"points": [v(0, 4000) * mm, v(-250, 4500) * mm, v(0, 6881.46) * mm], "startDerivative": vector(0, 2302.24) * mm, "endDerivative": vector(0, 5298.17) * mm});
            skFitSpline(sketch, "E117", {"points": [v(0, 4000) * mm, v(250, 4500) * mm, v(0, 6881.46) * mm], "startDerivative": vector(0, 2302.24) * mm, "endDerivative": vector(0, 5298.17) * mm});
            skSolve(sketch);
        }
        {
            var Q0;
            Q0=sQuery(id+"F61.wireOp",EDGE,"E112");
            cPlane(context, id + "F66", {"entities" : qUnion([Q0]), "cplaneType" : CPlaneType.LINE_ANGLE, "offset" : 25 * mm, "angle" : 180 * degree, "width" : 150 * mm, "height" : 150 * mm});
        }
        {
            var Q0;
            Q0=qCreatedBy(id+"F66.planeOp",FACE);
            var sketch = newSketch(context, id + "F67", { "sketchPlane" : qUnion([Q0])});
            skFitSpline(sketch, "E118", {"points": [v(0, 5943.2) * mm, v(-25, 6795.9) * mm, v(0, 7648.6) * mm], "startDerivative": vector(-75, 1705.4) * mm, "endDerivative": vector(75, 1705.4) * mm});
            skFitSpline(sketch, "E119", {"points": [v(0, 5943.2) * mm, v(25, 6795.9) * mm, v(0, 7648.6) * mm], "startDerivative": vector(75, 1705.4) * mm, "endDerivative": vector(-75, 1705.4) * mm});
            skSolve(sketch);
        }
        {
            var Q0;
            Q0=qCreatedBy(makeId("Front.planeOp"),FACE);
            cPlane(context, id + "F68", {"entities" : qUnion([Q0]), "cplaneType" : CPlaneType.OFFSET, "offset" : 8500 * mm, "oppositeDirection" : true, "width" : 150 * mm, "height" : 150 * mm});
        }
        {
            var Q0;
            Q0=qCreatedBy(id+"F68.planeOp",FACE);
            var sketch = newSketch(context, id + "F69", { "sketchPlane" : qUnion([Q0])});
            skCircle(sketch, "E120", {"center": v(0, 2775) * mm, "radius": 25 * mm});
            skSolve(sketch);
        }
        {
            var Q0;
            Q0=qCreatedBy(makeId("Right.planeOp"),FACE);
            var sketch = newSketch(context, id + "F70", { "sketchPlane" : qUnion([Q0])});
            skLineSegment(sketch, "E121", {"start": v(5943.2, 2572.89) * mm, "end": v(8500, 2800) * mm});
            skSolve(sketch);
        }
        {
            var Q1;
            Q1=qSketchRegion(id+"F63",true);
            var Q2;
            Q2=qSketchRegion(id+"F65",true);
            loft(context, id + "F71", {"sheetProfilesArray" : [{ "sheetProfileEntities" : qUnion([Q1]) }, { "sheetProfileEntities" : qUnion([Q2]) }]});
        }
        {
            var Q1;
            {var subQ0=sQuery(id+"F65.wireOp",EDGE,"E116");Q1=makeQuery(id+"F71.opLoft","CAP_FACE",FACE,{"disambiguationData":[OSD([makeQuery(id+"F65.imprint","IMPRINT",FACE,{"disambiguationData":[TD([[makeQuery(id+"F65.imprint","IMPRINT",EDGE,{"derivedFrom":subQ0}),-1.0]])]})])],"isStart":true});}
            var Q2;
            Q2=makeQuery(id+"F67.imprint","IMPRINT",FACE,{"disambiguationData":[TD([[makeQuery(id+"F67.imprint","IMPRINT",EDGE,{"derivedFrom":sQuery(id+"F67.wireOp",EDGE,"E118")}),-1.0]])]});
            loft(context, id + "F72", {"operationType" : NewBodyOperationType.ADD, "sheetProfilesArray" : [{ "sheetProfileEntities" : qUnion([Q1]) }, { "sheetProfileEntities" : qUnion([Q2]) }]});
        }
        {
            var Q1;
            Q1=makeQuery(id+"F72.opLoft","CAP_FACE",FACE,{"disambiguationData":[OSD([makeQuery(id+"F67.imprint","IMPRINT",FACE,{"disambiguationData":[TD([[makeQuery(id+"F67.imprint","IMPRINT",EDGE,{"derivedFrom":sQuery(id+"F67.wireOp",EDGE,"E118")}),-1.0]])]})])],"isStart":true});
            var Q2;
            Q2=makeQuery(id+"F69.imprint","IMPRINT",FACE,{"disambiguationData":[TD([[makeQuery(id+"F69.imprint","IMPRINT",EDGE,{"derivedFrom":sQuery(id+"F69.wireOp",EDGE,"E120")}),1.0]])]});
            var Q3;
            Q3=sQuery(id+"F70.wireOp",EDGE,"E121");
            loft(context, id + "F73", {"operationType" : NewBodyOperationType.ADD, "addGuides" : true, "sheetProfilesArray" : [{ "sheetProfileEntities" : qUnion([Q1]) }, { "sheetProfileEntities" : qUnion([Q2]) }], "guidesArray" : [{ "guideEntities" : qUnion([Q3]), "guideDerivativeType" : LoftGuideDerivativeType.DEFAULT, "guideDerivativeMagnitude" : 1 }]});
        }
        {
            var Q0;
            Q0=qCreatedBy(makeId("Top.planeOp"),FACE);
            cPlane(context, id + "F74", {"entities" : qUnion([Q0]), "cplaneType" : CPlaneType.OFFSET, "offset" : 2000 * mm, "width" : 150 * mm, "height" : 150 * mm});
        }
        {
            var Q0;
            Q0=qCreatedBy(id+"F74.planeOp",FACE);
            var sketch = newSketch(context, id + "F75", { "sketchPlane" : qUnion([Q0])});
            skLineSegment(sketch, "E122", {"start": v(0, 0) * mm, "end": v(0, 4500) * mm});
            skLineSegment(sketch, "E123", {"start": v(0, 4500) * mm, "end": v(0, 7369.2) * mm});
            skLineSegment(sketch, "E124", {"start": v(0, 7369.2) * mm, "end": v(0, 5235.43) * mm});
            skLineSegment(sketch, "E125", {"start": v(0, 6302.31) * mm, "end": v(0, 5302.31) * mm});
            skLineSegment(sketch, "E126", {"start": v(0, 6302.31) * mm, "end": v(0, 7302.31) * mm});
            skLineSegment(sketch, "E127", {"start": v(0, 6302.31) * mm, "end": v(0, 6552.31) * mm});
            skLineSegment(sketch, "E128", {"start": v(0, 6302.31) * mm, "end": v(-1200, 6302.31) * mm});
            skLineSegment(sketch, "E129", {"start": v(0, 6302.31) * mm, "end": v(1200, 6302.31) * mm});
            skLineSegment(sketch, "E130", {"start": v(0, 6552.31) * mm, "end": v(-1700, 6552.31) * mm});
            skLineSegment(sketch, "E131", {"start": v(0, 6552.31) * mm, "end": v(1700, 6552.31) * mm});
            skLineSegment(sketch, "E132", {"start": v(0, 7302.31) * mm, "end": v(-2000, 7302.31) * mm});
            skLineSegment(sketch, "E133", {"start": v(0, 7302.31) * mm, "end": v(2000, 7302.31) * mm});
            skLineSegment(sketch, "E134", {"start": v(-2000, 7302.31) * mm, "end": v(-2000, 7052.31) * mm});
            skLineSegment(sketch, "E135", {"start": v(2000, 7302.31) * mm, "end": v(2000, 7052.31) * mm});
            skFitSpline(sketch, "E136", {"points": [v(0, 5302.31) * mm, v(-1200, 6302.31) * mm, v(-2000, 7052.31) * mm], "startDerivative": vector(0, 5513.6) * mm, "endDerivative": vector(-1974.16, 3290.27) * mm});
            skFitSpline(sketch, "E137", {"points": [v(0, 5302.31) * mm, v(1200, 6302.31) * mm, v(2000, 7052.31) * mm], "startDerivative": vector(0, 5513.6) * mm, "endDerivative": vector(1974.16, 3290.27) * mm});
            skFitSpline(sketch, "E138", {"points": [v(0, 6552.31) * mm, v(-2000, 7302.31) * mm], "startDerivative": vector(0, 2250) * mm, "endDerivative": vector(-900, 2250) * mm});
            skFitSpline(sketch, "E139", {"points": [v(0, 6552.31) * mm, v(2000, 7302.31) * mm], "startDerivative": vector(0, 2250) * mm, "endDerivative": vector(900, 2250) * mm});
            skSolve(sketch);
        }
        {
            var Q0;
            Q0=qCreatedBy(makeId("Right.planeOp"),FACE);
            var sketch = newSketch(context, id + "F76", { "sketchPlane" : qUnion([Q0])});
            skFitSpline(sketch, "E140", {"points": [v(5302.31, 2000) * mm, v(5927.31, 2050) * mm, v(6552.31, 2000) * mm], "startDerivative": vector(1250, 150) * mm, "endDerivative": vector(1250, -150) * mm});
            skFitSpline(sketch, "E141", {"points": [v(5302.31, 2000) * mm, v(5927.31, 1950) * mm, v(6552.31, 2000) * mm], "startDerivative": vector(1250, -150) * mm, "endDerivative": vector(1250, 150) * mm});
            skSolve(sketch);
        }
        {
            var Q0;
            Q0=qCreatedBy(makeId("Right.planeOp"),FACE);
            cPlane(context, id + "F77", {"entities" : qUnion([Q0]), "cplaneType" : CPlaneType.OFFSET, "offset" : 2000 * mm, "oppositeDirection" : true, "width" : 150 * mm, "height" : 150 * mm});
        }
        {
            var Q0;
            Q0=qCreatedBy(id+"F77.planeOp",FACE);
            var sketch = newSketch(context, id + "F78", { "sketchPlane" : qUnion([Q0])});
            skFitSpline(sketch, "E142", {"points": [v(7052.31, 2000) * mm, v(7177.31, 2010) * mm, v(7302.31, 2000) * mm], "startDerivative": vector(250, 30) * mm, "endDerivative": vector(250, -30) * mm});
            skFitSpline(sketch, "E143", {"points": [v(7052.31, 2000) * mm, v(7177.31, 1990) * mm, v(7302.31, 2000) * mm], "startDerivative": vector(250, -30) * mm, "endDerivative": vector(250, 30) * mm});
            skSolve(sketch);
        }
        {
            var Q0;
            Q0=qCreatedBy(makeId("Right.planeOp"),FACE);
            cPlane(context, id + "F79", {"entities" : qUnion([Q0]), "cplaneType" : CPlaneType.OFFSET, "offset" : 2000 * mm, "width" : 150 * mm, "height" : 150 * mm});
        }
        {
            var Q0;
            Q0=qCreatedBy(id+"F79.planeOp",FACE);
            var sketch = newSketch(context, id + "F80", { "sketchPlane" : qUnion([Q0])});
            skFitSpline(sketch, "E144", {"points": [v(7052.31, 2000) * mm, v(7177.31, 2010) * mm, v(7302.31, 2000) * mm], "startDerivative": vector(250, 30) * mm, "endDerivative": vector(250, -30) * mm});
            skFitSpline(sketch, "E145", {"points": [v(7052.31, 2000) * mm, v(7177.31, 1990) * mm, v(7302.31, 2000) * mm], "startDerivative": vector(250, -30) * mm, "endDerivative": vector(250, 30) * mm});
            skSolve(sketch);
        }
        {
            var Q1;
            Q1=qSketchRegion(id+"F76",true);
            var Q2;
            Q2=makeQuery(id+"F78.imprint","IMPRINT",FACE,{"disambiguationData":[TD([[makeQuery(id+"F78.imprint","IMPRINT",EDGE,{"derivedFrom":sQuery(id+"F78.wireOp",EDGE,"E142")}),-1.0]])]});
            var Q3;
            Q3=sQuery(id+"F75.wireOp",EDGE,"E136");
            var Q4;
            Q4=sQuery(id+"F75.wireOp",EDGE,"E138");
            loft(context, id + "F81", {"addGuides" : true, "sheetProfilesArray" : [{ "sheetProfileEntities" : qUnion([Q1]) }, { "sheetProfileEntities" : qUnion([Q2]) }], "guidesArray" : [{ "guideEntities" : qUnion([Q3]), "guideDerivativeType" : LoftGuideDerivativeType.DEFAULT, "guideDerivativeMagnitude" : 1 }, { "guideEntities" : qUnion([Q4]), "guideDerivativeType" : LoftGuideDerivativeType.DEFAULT, "guideDerivativeMagnitude" : 1 }]});
        }
        {
            var Q1;
            Q1=qSketchRegion(id+"F76",true);
            var Q2;
            Q2=makeQuery(id+"F80.imprint","IMPRINT",FACE,{"disambiguationData":[TD([[makeQuery(id+"F80.imprint","IMPRINT",EDGE,{"derivedFrom":sQuery(id+"F80.wireOp",EDGE,"E144")}),-1.0]])]});
            var Q3;
            Q3=sQuery(id+"F75.wireOp",EDGE,"E137");
            var Q4;
            Q4=sQuery(id+"F75.wireOp",EDGE,"E139");
            loft(context, id + "F82", {"operationType" : NewBodyOperationType.ADD, "addGuides" : true, "sheetProfilesArray" : [{ "sheetProfileEntities" : qUnion([Q1]) }, { "sheetProfileEntities" : qUnion([Q2]) }], "guidesArray" : [{ "guideEntities" : qUnion([Q3]), "guideDerivativeType" : LoftGuideDerivativeType.DEFAULT, "guideDerivativeMagnitude" : 1 }, { "guideEntities" : qUnion([Q4]), "guideDerivativeType" : LoftGuideDerivativeType.DEFAULT, "guideDerivativeMagnitude" : 1 }]});
        }
    });
